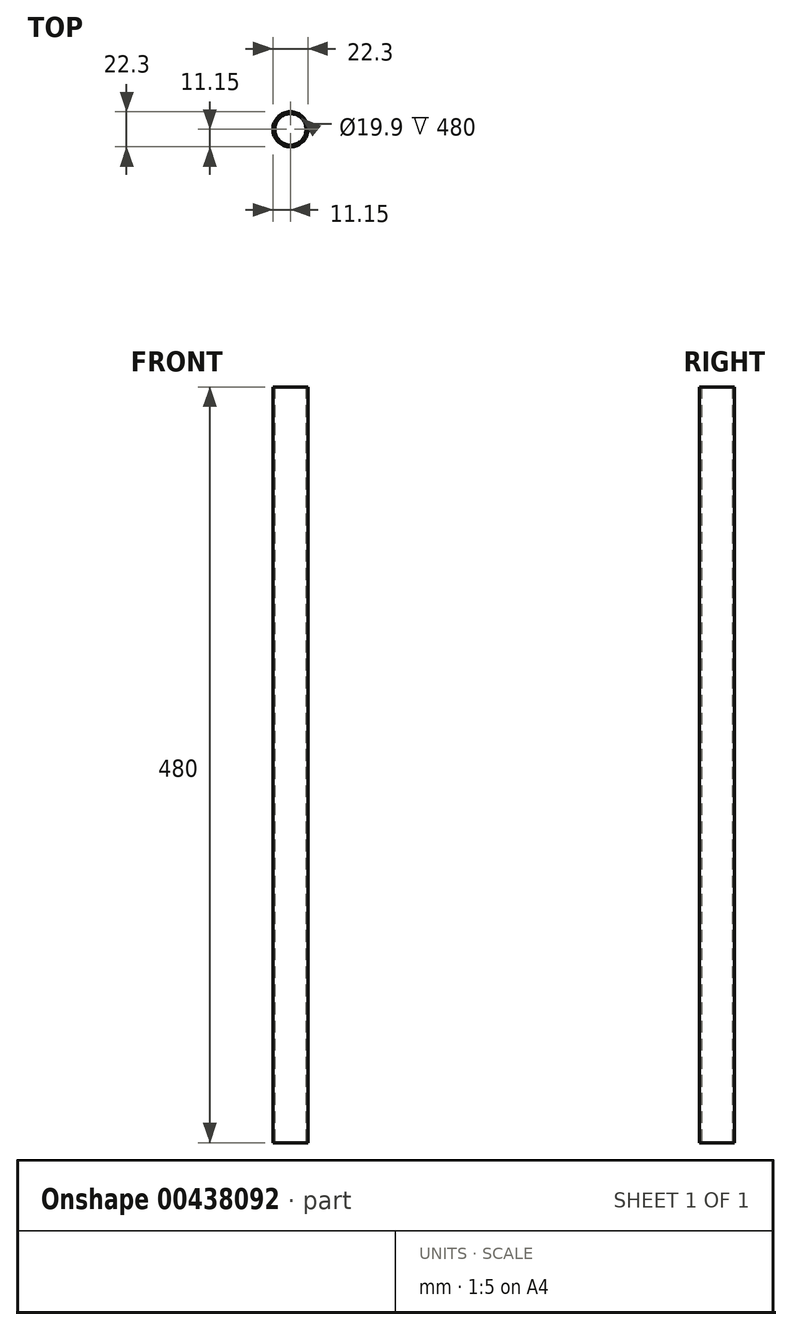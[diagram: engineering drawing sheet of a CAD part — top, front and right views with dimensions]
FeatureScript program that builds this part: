
annotation { "Feature Type Name" : "Feature", "Feature Type Description" : "" }
export const myFeature = defineFeature(function(context is Context, id is Id, definition is map)
    precondition{}
    {
        {
            var Q0;
            Q0=qCreatedBy(makeId("Top.planeOp"),FACE);
            var sketch = newSketch(context, id + "F0", { "sketchPlane" : qUnion([Q0])});
            skCircle(sketch, "E0", {"center": v(0, 0) * mm, "radius": 11.15 * mm});
            skCircle(sketch, "E1.0", {"center": v(0, 0) * mm, "radius": 9.95 * mm});
            skSolve(sketch);
        }
        {
            var Q0;
            Q0 = qSketchRegion(id + "F0", true);
            extrude(context, id + "F1", {"entities" : qUnion([Q0]), "depth" : 480 * mm});
        }
    });
